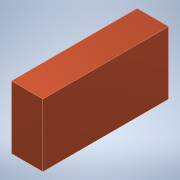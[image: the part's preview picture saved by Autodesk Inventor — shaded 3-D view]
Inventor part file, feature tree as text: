
AUTODESK INVENTOR PART (.ipt)
format: ipt  version: 2022 (Build 260153000, 153)  size: 93,184 bytes
history: native  units: mm
features: extrude x1, sketch x1
ambient origin geometry x8: Origin, YZ Plane, XZ Plane, XY Plane, X Axis, Y Axis, Z Axis, Center Point
bodies: Solid1 (feature_tree)
feature tree (2):
  extrude  "Extrusion1"  Depth=5.0mm TaperAngle=0.0deg
  sketch  "Sketch1"  dims[d0=10.0mm d1=5.0mm d2=0.0mm]
